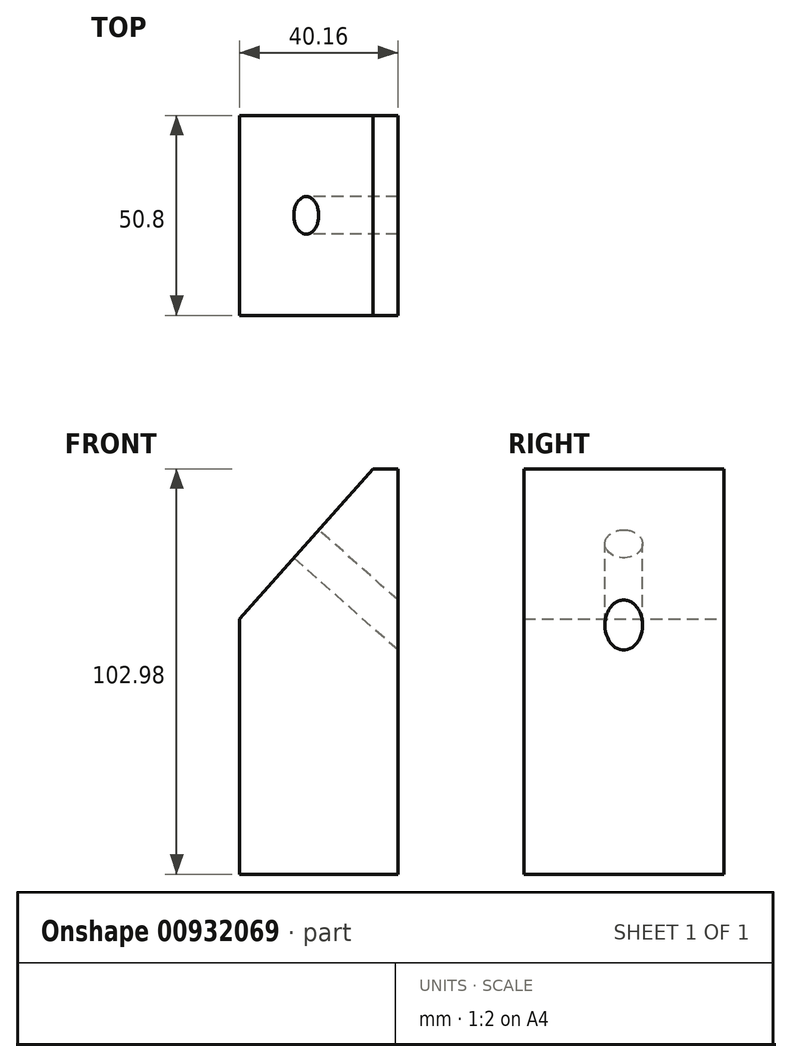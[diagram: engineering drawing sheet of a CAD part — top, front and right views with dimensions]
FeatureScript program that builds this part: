
annotation { "Feature Type Name" : "Feature", "Feature Type Description" : "" }
export const myFeature = defineFeature(function(context is Context, id is Id, definition is map)
    precondition{}
    {
        {
            var Q0;
            Q0=qCreatedBy(makeId("Front.planeOp"),FACE);
            var sketch = newSketch(context, id + "F0", { "sketchPlane" : qUnion([Q0])});
            skLineSegment(sketch, "E0", {"start": v(0, 0) * mm, "end": v(0, 64.88) * mm});
            skLineSegment(sketch, "E1", {"start": v(0, 64.88) * mm, "end": v(33.81, 102.98) * mm});
            skLineSegment(sketch, "E2", {"start": v(33.81, 102.98) * mm, "end": v(40.16, 102.98) * mm});
            skLineSegment(sketch, "E3", {"start": v(40.16, 102.98) * mm, "end": v(40.16, 0) * mm});
            skLineSegment(sketch, "E4", {"start": v(40.16, 0) * mm, "end": v(0, 0) * mm});
            skSolve(sketch);
        }
        {
            var Q0;
            Q0 = qSketchRegion(id + "F0", true);
            extrude(context, id + "F1", {"entities" : qUnion([Q0]), "depth" : 50.8 * mm, "offsetDistance" : 25.4 * mm});
        }
        {
            var Q0;
            Q0=makeQuery(id+"F1.opExtrude","SWEPT_FACE",FACE,{"disambiguationData":[OSD([sQuery(id+"F0.wireOp",EDGE,"E1")])]});
            var sketch = newSketch(context, id + "F2", { "sketchPlane" : qUnion([Q0])});
            skCircle(sketch, "E5", {"center": v(25.4, 74) * mm, "radius": 4.76 * mm});
            skPoint(sketch, "E5.centerSnap0", {"position": v(25.4, 99.46) * mm});
            skSolve(sketch);
        }
        {
            var Q0;
            Q0 = qSketchRegion(id + "F2", true);
            extrude(context, id + "F3", {"entities" : qUnion([Q0]), "operationType" : NewBodyOperationType.REMOVE, "endBound" : BoundingType.THROUGH_ALL, "oppositeDirection" : true, "depth" : 25.4 * mm, "offsetDistance" : 25.4 * mm});
        }
    });
